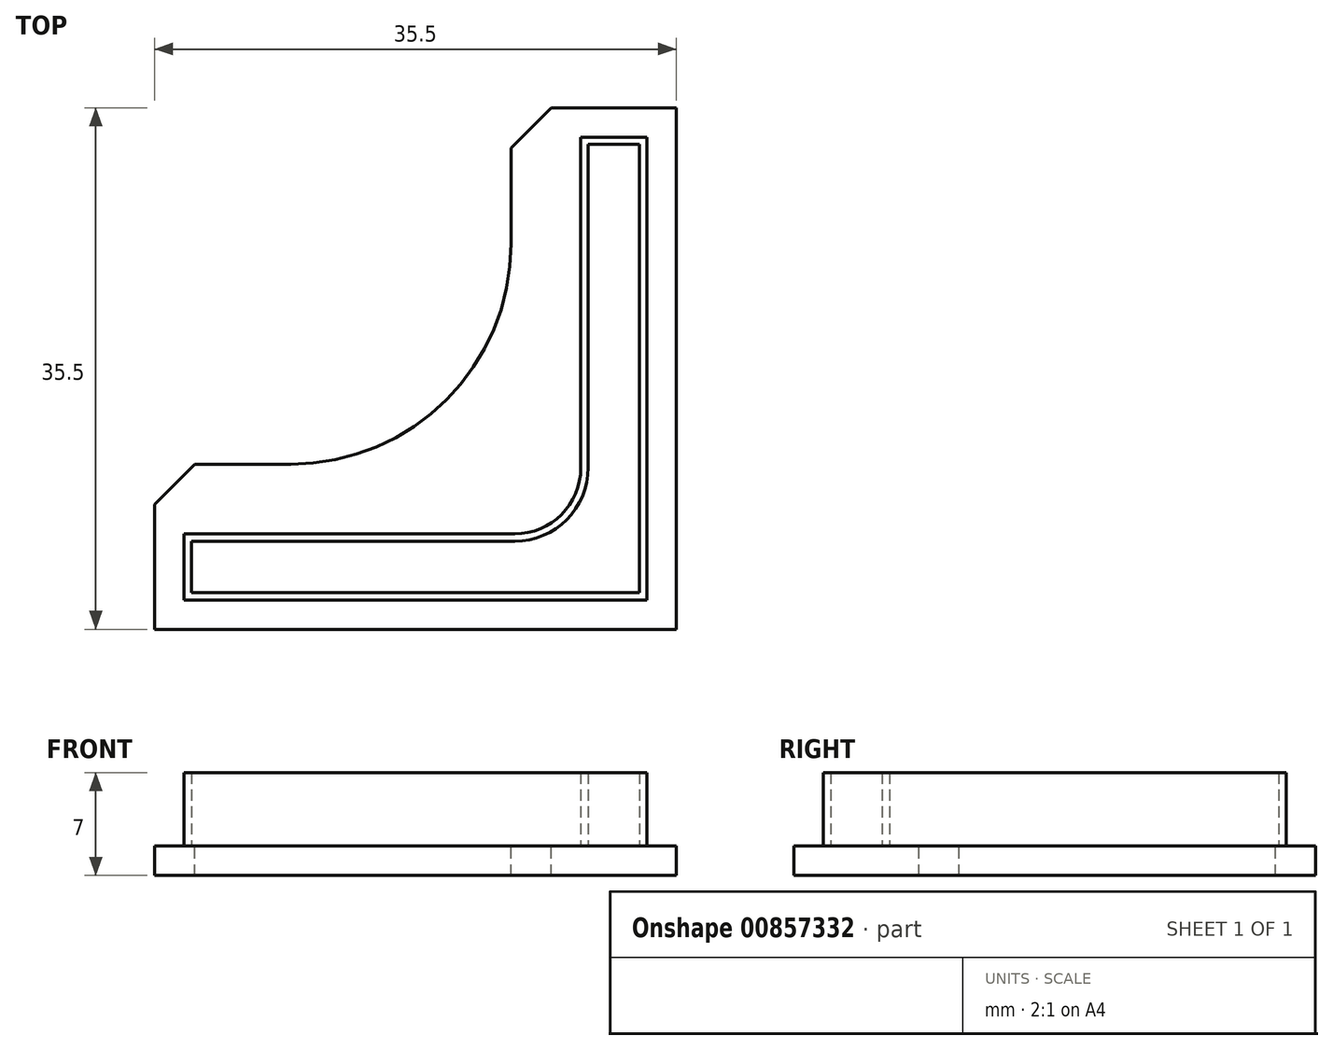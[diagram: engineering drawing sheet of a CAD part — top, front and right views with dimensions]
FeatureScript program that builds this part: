
annotation { "Feature Type Name" : "Feature", "Feature Type Description" : "" }
export const myFeature = defineFeature(function(context is Context, id is Id, definition is map)
    precondition{}
    {
        {
            var Q0;
            Q0=qCreatedBy(makeId("Top.planeOp"),FACE);
            var sketch = newSketch(context, id + "F0", { "sketchPlane" : qUnion([Q0])});
            skLineSegment(sketch, "E0", {"start": v(-5, 0) * mm, "end": v(-27, 0) * mm});
            skLineSegment(sketch, "E1", {"start": v(-27, 0) * mm, "end": v(-27, -3.5) * mm});
            skLineSegment(sketch, "E2", {"start": v(-27, -3.5) * mm, "end": v(3.5, -3.5) * mm});
            skLineSegment(sketch, "E3", {"start": v(3.5, -3.5) * mm, "end": v(3.5, 27) * mm});
            skLineSegment(sketch, "E4", {"start": v(3.5, 27) * mm, "end": v(0, 27) * mm});
            skLineSegment(sketch, "E5", {"start": v(0, 27) * mm, "end": v(0, 5) * mm});
            skLineSegment(sketch, "E6.0", {"start": v(4, 27.5) * mm, "end": v(-0.5, 27.5) * mm});
            skLineSegment(sketch, "E6.1", {"start": v(-5, 0.5) * mm, "end": v(-27.5, 0.5) * mm});
            skLineSegment(sketch, "E6.2", {"start": v(-27.5, 0.5) * mm, "end": v(-27.5, -4) * mm});
            skLineSegment(sketch, "E6.3", {"start": v(-0.5, 27.5) * mm, "end": v(-0.5, 5) * mm});
            skLineSegment(sketch, "E6.4", {"start": v(-27.5, -4) * mm, "end": v(4, -4) * mm});
            skLineSegment(sketch, "E6.5", {"start": v(4, -4) * mm, "end": v(4, 27.5) * mm});
            skPoint(sketch, "E7.visualSharp", {"position": v(-0.5, 0.5) * mm});
            skArc(sketch, "E7.filletArc", {"start": v(-5, 0.5) * mm, "mid": v(-1.82, 1.82) * mm, "end": v(-0.5, 5) * mm});
            skPoint(sketch, "E8.visualSharp", {"position": v(0, 0) * mm});
            skArc(sketch, "E8.filletArc", {"start": v(-5, 0) * mm, "mid": v(-1.46, 1.46) * mm, "end": v(0, 5) * mm});
            skSolve(sketch);
        }
        {
            var Q0;
            Q0 = qSketchRegion(id + "F0", true);
            extrude(context, id + "F1", {"entities" : qUnion([Q0]), "depth" : 5 * mm, "offsetDistance" : 25 * mm});
        }
        {
            var Q0;
            Q0=qCreatedBy(makeId("Top.planeOp"),FACE);
            var sketch = newSketch(context, id + "F2", { "sketchPlane" : qUnion([Q0])});
            skLineSegment(sketch, "E9.bottom", {"start": v(6, -6) * mm, "end": v(-29.5, -6) * mm});
            skLineSegment(sketch, "E9.left", {"start": v(6, -6) * mm, "end": v(6, 29.5) * mm});
            skLineSegment(sketch, "E10", {"start": v(-29.5, -6) * mm, "end": v(-29.5, 2.5) * mm});
            skLineSegment(sketch, "E11", {"start": v(-29.5, 2.5) * mm, "end": v(-2.5, 29.5) * mm});
            skLineSegment(sketch, "E12", {"start": v(6, 29.5) * mm, "end": v(-2.5, 29.5) * mm});
            skLineSegment(sketch, "E13", {"start": v(-16, 16) * mm, "end": v(-25.13, 25.13) * mm, "construction": true});
            skArc(sketch, "E14", {"start": v(-6.28, 25.72) * mm, "mid": v(-9.64, 9.64) * mm, "end": v(-25.72, 6.28) * mm});
            skLineSegment(sketch, "E15", {"start": v(-5.24, 26.76) * mm, "end": v(-5.24, 20.24) * mm});
            skLineSegment(sketch, "E16", {"start": v(-26.76, 5.24) * mm, "end": v(-20.24, 5.24) * mm});
            skSolve(sketch);
        }
        {
            var Q0;
            Q0=makeQuery(id+"F2.imprint","IMPRINT",FACE,{"disambiguationData":[TD([[makeQuery(id+"F2.imprint","IMPRINT",EDGE,{"derivedFrom":sQuery(id+"F2.wireOp",EDGE,"E9.bottom")}),-1.0]])]});
            extrude(context, id + "F3", {"entities" : qUnion([Q0]), "operationType" : NewBodyOperationType.ADD, "oppositeDirection" : true, "depth" : 2 * mm, "offsetDistance" : 25 * mm});
        }
    });
